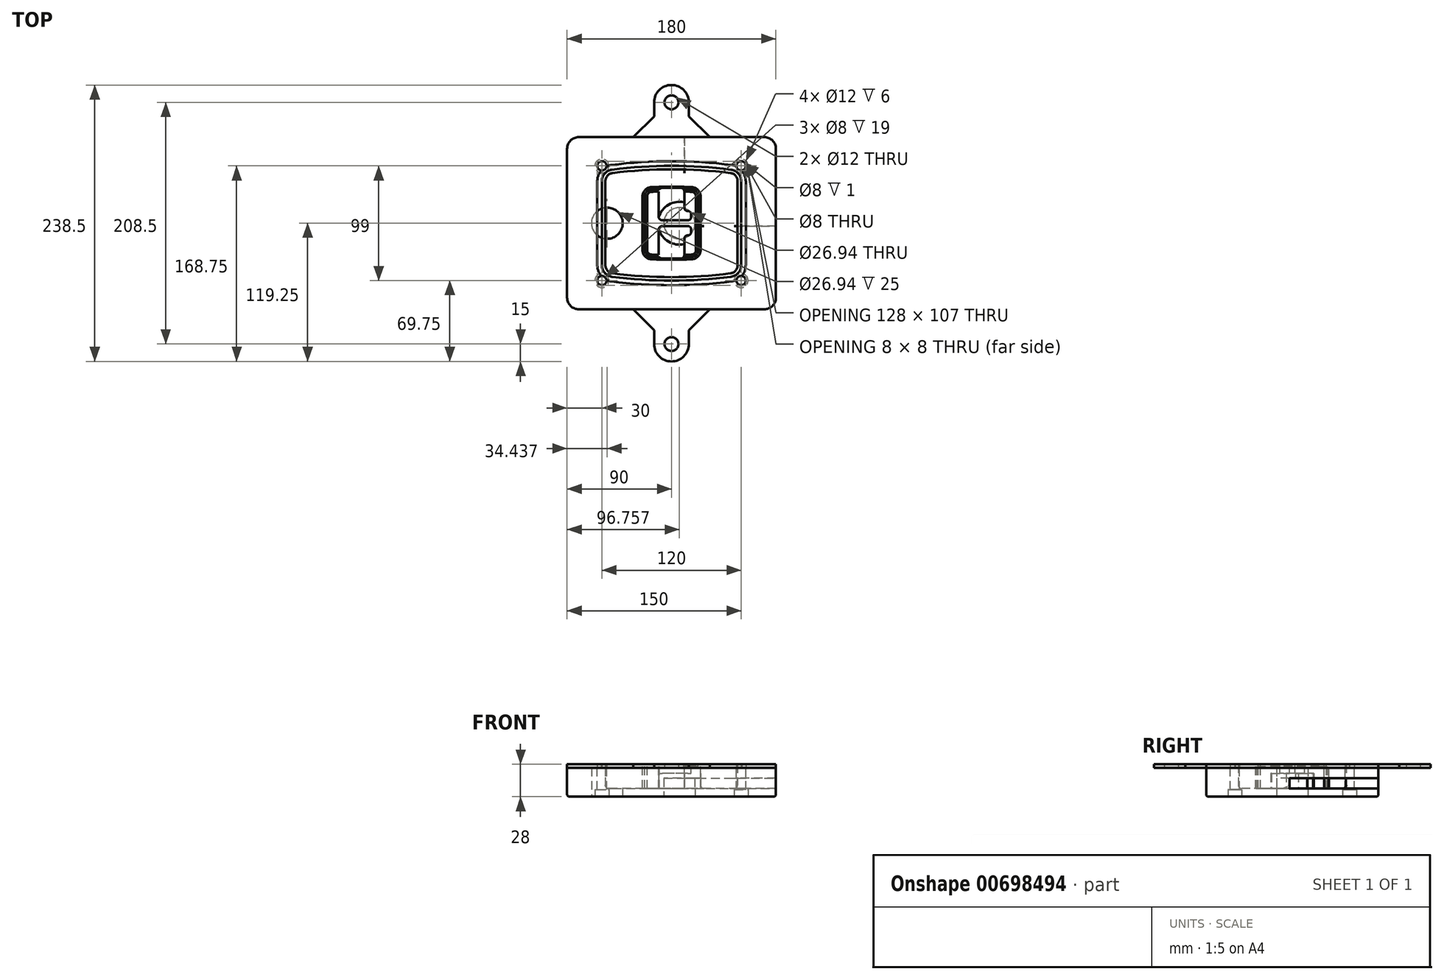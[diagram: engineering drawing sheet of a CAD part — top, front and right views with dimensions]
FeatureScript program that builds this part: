
annotation { "Feature Type Name" : "Feature", "Feature Type Description" : "" }
export const myFeature = defineFeature(function(context is Context, id is Id, definition is map)
    precondition{}
    {
        {
            var Q0;
            Q0=qCreatedBy(makeId("Top.planeOp"),FACE);
            var sketch = newSketch(context, id + "F0", { "sketchPlane" : qUnion([Q0])});
            skPoint(sketch, "E0.rect.middle", {"position": v(0, 0) * mm});
            skLineSegment(sketch, "E1.bottom", {"start": v(-80, -74.25) * mm, "end": v(80, -74.25) * mm});
            skLineSegment(sketch, "E1.top", {"start": v(-80, 74.25) * mm, "end": v(80, 74.25) * mm});
            skLineSegment(sketch, "E1.left", {"start": v(-90, -64.25) * mm, "end": v(-90, 64.25) * mm});
            skLineSegment(sketch, "E1.right", {"start": v(90, -64.25) * mm, "end": v(90, 64.25) * mm});
            skLineSegment(sketch, "E2", {"start": v(-90, 74.25) * mm, "end": v(90, -74.25) * mm, "construction": true});
            skLineSegment(sketch, "E3", {"start": v(90, 74.25) * mm, "end": v(-90, -74.25) * mm, "construction": true});
            skCircle(sketch, "E4", {"center": v(-60, 49.5) * mm, "radius": 4 * mm});
            skCircle(sketch, "E5", {"center": v(60, 49.5) * mm, "radius": 4 * mm});
            skCircle(sketch, "E6", {"center": v(60, -49.5) * mm, "radius": 4 * mm});
            skCircle(sketch, "E7", {"center": v(-60, -49.5) * mm, "radius": 4 * mm});
            skLineSegment(sketch, "E8", {"start": v(-60, 49.5) * mm, "end": v(60, 49.5) * mm, "construction": true});
            skLineSegment(sketch, "E9", {"start": v(60, 49.5) * mm, "end": v(60, -49.5) * mm, "construction": true});
            skLineSegment(sketch, "E10", {"start": v(60, -49.5) * mm, "end": v(-60, -49.5) * mm, "construction": true});
            skLineSegment(sketch, "E11", {"start": v(-60, -49.5) * mm, "end": v(-60, 49.5) * mm, "construction": true});
            skLineSegment(sketch, "E12", {"start": v(-60, 36.3) * mm, "end": v(-60, -36.3) * mm});
            skLineSegment(sketch, "E13", {"start": v(60, 36.3) * mm, "end": v(60, -36.3) * mm});
            skArc(sketch, "E14", {"start": v(51.27, 46.22) * mm, "mid": v(0, 49.5) * mm, "end": v(-51.27, 46.22) * mm});
            skArc(sketch, "E15", {"start": v(-51.27, -46.22) * mm, "mid": v(0, -49.5) * mm, "end": v(51.27, -46.22) * mm});
            skLineSegment(sketch, "E16", {"start": v(-60, 0) * mm, "end": v(60, 0) * mm, "construction": true});
            skPoint(sketch, "E17.visualSharp", {"position": v(-60, -45) * mm});
            skArc(sketch, "E17.filletArc", {"start": v(-60, -36.3) * mm, "mid": v(-57.5, -42.9) * mm, "end": v(-51.27, -46.22) * mm});
            skPoint(sketch, "E18.visualSharp", {"position": v(-60, 45) * mm});
            skArc(sketch, "E18.filletArc", {"start": v(-51.27, 46.22) * mm, "mid": v(-57.5, 42.9) * mm, "end": v(-60, 36.3) * mm});
            skPoint(sketch, "E19.visualSharp", {"position": v(60, 45) * mm});
            skArc(sketch, "E19.filletArc", {"start": v(60, 36.3) * mm, "mid": v(57.5, 42.9) * mm, "end": v(51.27, 46.22) * mm});
            skPoint(sketch, "E20.visualSharp", {"position": v(60, -45) * mm});
            skArc(sketch, "E20.filletArc", {"start": v(51.27, -46.22) * mm, "mid": v(57.5, -42.9) * mm, "end": v(60, -36.3) * mm});
            skPoint(sketch, "E21.visualSharp", {"position": v(-90, 74.25) * mm});
            skArc(sketch, "E21.filletArc", {"start": v(-80, 74.25) * mm, "mid": v(-87.07, 71.32) * mm, "end": v(-90, 64.25) * mm});
            skPoint(sketch, "E22.visualSharp", {"position": v(90, 74.25) * mm});
            skArc(sketch, "E22.filletArc", {"start": v(90, 64.25) * mm, "mid": v(87.07, 71.32) * mm, "end": v(80, 74.25) * mm});
            skPoint(sketch, "E23.visualSharp", {"position": v(90, -74.25) * mm});
            skArc(sketch, "E23.filletArc", {"start": v(80, -74.25) * mm, "mid": v(87.07, -71.32) * mm, "end": v(90, -64.25) * mm});
            skPoint(sketch, "E24.visualSharp", {"position": v(-90, -74.25) * mm});
            skArc(sketch, "E24.filletArc", {"start": v(-90, -64.25) * mm, "mid": v(-87.07, -71.32) * mm, "end": v(-80, -74.25) * mm});
            skArc(sketch, "E25.0", {"start": v(57, 36.3) * mm, "mid": v(55.26, 40.92) * mm, "end": v(50.9, 43.24) * mm});
            skLineSegment(sketch, "E25.1", {"start": v(57, 36.3) * mm, "end": v(57, -36.3) * mm});
            skArc(sketch, "E25.2", {"start": v(50.9, -43.24) * mm, "mid": v(55.26, -40.92) * mm, "end": v(57, -36.3) * mm});
            skArc(sketch, "E25.3", {"start": v(-50.9, -43.24) * mm, "mid": v(0, -46.5) * mm, "end": v(50.9, -43.24) * mm});
            skArc(sketch, "E25.4", {"start": v(-57, -36.3) * mm, "mid": v(-55.26, -40.92) * mm, "end": v(-50.9, -43.24) * mm});
            skArc(sketch, "E25.5", {"start": v(50.9, 43.24) * mm, "mid": v(0, 46.5) * mm, "end": v(-50.9, 43.24) * mm});
            skLineSegment(sketch, "E25.6", {"start": v(-57, 36.3) * mm, "end": v(-57, -36.3) * mm});
            skArc(sketch, "E25.7", {"start": v(-50.9, 43.24) * mm, "mid": v(-55.26, 40.92) * mm, "end": v(-57, 36.3) * mm});
            skArc(sketch, "E26.0", {"start": v(-51.78, 50.19) * mm, "mid": v(-60.51, 45.55) * mm, "end": v(-64, 36.3) * mm});
            skArc(sketch, "E26.1", {"start": v(51.78, 50.19) * mm, "mid": v(0, 53.5) * mm, "end": v(-51.78, 50.19) * mm});
            skArc(sketch, "E26.2", {"start": v(64, 36.3) * mm, "mid": v(60.51, 45.55) * mm, "end": v(51.78, 50.19) * mm});
            skLineSegment(sketch, "E26.3", {"start": v(64, 36.3) * mm, "end": v(64, -36.3) * mm});
            skArc(sketch, "E26.4", {"start": v(51.78, -50.19) * mm, "mid": v(60.51, -45.55) * mm, "end": v(64, -36.3) * mm});
            skLineSegment(sketch, "E26.5", {"start": v(-64, 36.3) * mm, "end": v(-64, -36.3) * mm});
            skArc(sketch, "E26.6", {"start": v(-51.78, -50.19) * mm, "mid": v(0, -53.5) * mm, "end": v(51.78, -50.19) * mm});
            skArc(sketch, "E26.7", {"start": v(-64, -36.3) * mm, "mid": v(-60.51, -45.55) * mm, "end": v(-51.78, -50.19) * mm});
            skSolve(sketch);
        }
        {
            var Q0;
            Q0=makeQuery(id+"F0.imprint","IMPRINT",FACE,{"disambiguationData":[TD([[makeQuery(id+"F0.imprint","IMPRINT",EDGE,{"derivedFrom":sQuery(id+"F0.wireOp",EDGE,"E1.bottom")}),1.0]])]});
            var Q1;
            Q1=makeQuery(id+"F0.imprint","IMPRINT",FACE,{"disambiguationData":[TD([[makeQuery(id+"F0.imprint","IMPRINT",EDGE,{"derivedFrom":sQuery(id+"F0.wireOp",EDGE,"E12")}),1.0]])]});
            var Q2;
            Q2=makeQuery(id+"F0.imprint","IMPRINT",FACE,{"disambiguationData":[TD([[makeQuery(id+"F0.imprint","IMPRINT",EDGE,{"derivedFrom":sQuery(id+"F0.wireOp",EDGE,"E25.0")}),1.0]])]});
            var Q3;
            Q3=makeQuery(id+"F0.imprint","IMPRINT",FACE,{"disambiguationData":[TD([[makeQuery(id+"F0.imprint","IMPRINT",EDGE,{"derivedFrom":sQuery(id+"F0.wireOp",EDGE,"E12")}),-1.0]])]});
            extrude(context, id + "F1", {"entities" : qUnion([Q0, Q1, Q2, Q3]), "oppositeDirection" : true, "depth" : 25 * mm});
        }
        {
            var Q0;
            Q0=makeQuery(id+"F0.imprint","IMPRINT",FACE,{"disambiguationData":[TD([[makeQuery(id+"F0.imprint","IMPRINT",EDGE,{"derivedFrom":sQuery(id+"F0.wireOp",EDGE,"E12")}),1.0]])]});
            extrude(context, id + "F2", {"entities" : qUnion([Q0]), "operationType" : NewBodyOperationType.ADD, "depth" : 3 * mm});
        }
        {
            var Q0;
            Q0=makeQuery(id+"F0.imprint","IMPRINT",FACE,{"disambiguationData":[TD([[makeQuery(id+"F0.imprint","IMPRINT",EDGE,{"derivedFrom":sQuery(id+"F0.wireOp",EDGE,"E25.0")}),1.0]])]});
            extrude(context, id + "F3", {"entities" : qUnion([Q0]), "operationType" : NewBodyOperationType.REMOVE, "oppositeDirection" : true, "depth" : 18 * mm});
        }
        {
            var Q0;
            Q0=makeQuery(id+"F2.opExtrude","CAP_FACE",FACE,{"disambiguationData":[OSD([sQuery(id+"F0.wireOp",EDGE,"E12"),sQuery(id+"F0.wireOp",EDGE,"E13"),sQuery(id+"F0.wireOp",EDGE,"E14"),sQuery(id+"F0.wireOp",EDGE,"E15"),sQuery(id+"F0.wireOp",EDGE,"E17.filletArc"),sQuery(id+"F0.wireOp",EDGE,"E18.filletArc"),sQuery(id+"F0.wireOp",EDGE,"E19.filletArc"),sQuery(id+"F0.wireOp",EDGE,"E20.filletArc"),sQuery(id+"F0.wireOp",EDGE,"E25.0"),sQuery(id+"F0.wireOp",EDGE,"E25.1"),sQuery(id+"F0.wireOp",EDGE,"E25.2"),sQuery(id+"F0.wireOp",EDGE,"E25.3"),sQuery(id+"F0.wireOp",EDGE,"E25.4"),sQuery(id+"F0.wireOp",EDGE,"E25.5"),sQuery(id+"F0.wireOp",EDGE,"E25.6"),sQuery(id+"F0.wireOp",EDGE,"E25.7")])],"isStart":false});
            var sketch = newSketch(context, id + "F4", { "sketchPlane" : qUnion([Q0])});
            skArc(sketch, "E27.0", {"start": v(-17.36, -31.1) * mm, "mid": v(0, -31.5) * mm, "end": v(17.36, -31.1) * mm});
            skArc(sketch, "E28.0", {"start": v(17.36, 31.1) * mm, "mid": v(0, 31.5) * mm, "end": v(-17.36, 31.1) * mm});
            skLineSegment(sketch, "E29", {"start": v(-25, 23.12) * mm, "end": v(-25, -23.12) * mm});
            skLineSegment(sketch, "E30", {"start": v(25, 23.12) * mm, "end": v(25, -23.12) * mm});
            skLineSegment(sketch, "E31", {"start": v(-25, 30.69) * mm, "end": v(25, 30.69) * mm, "construction": true});
            skLineSegment(sketch, "E32", {"start": v(-25, -30.69) * mm, "end": v(25, -30.69) * mm, "construction": true});
            skPoint(sketch, "E33.visualSharp", {"position": v(-25, 30.69) * mm});
            skArc(sketch, "E33.filletArc", {"start": v(-17.36, 31.1) * mm, "mid": v(-22.78, 28.64) * mm, "end": v(-25, 23.12) * mm});
            skPoint(sketch, "E34.visualSharp", {"position": v(25, 30.69) * mm});
            skArc(sketch, "E34.filletArc", {"start": v(25, 23.12) * mm, "mid": v(22.78, 28.64) * mm, "end": v(17.36, 31.1) * mm});
            skPoint(sketch, "E35.visualSharp", {"position": v(25, -30.69) * mm});
            skArc(sketch, "E35.filletArc", {"start": v(17.36, -31.1) * mm, "mid": v(22.78, -28.64) * mm, "end": v(25, -23.12) * mm});
            skPoint(sketch, "E36.visualSharp", {"position": v(-25, -30.69) * mm});
            skArc(sketch, "E36.filletArc", {"start": v(-25, -23.12) * mm, "mid": v(-22.78, -28.64) * mm, "end": v(-17.36, -31.1) * mm});
            skArc(sketch, "E37.0", {"start": v(50.9, 43.24) * mm, "mid": v(0, 46.5) * mm, "end": v(-50.9, 43.24) * mm});
            skArc(sketch, "E37.1", {"start": v(-50.9, 43.24) * mm, "mid": v(-55.26, 40.92) * mm, "end": v(-57, 36.3) * mm});
            skLineSegment(sketch, "E37.2", {"start": v(-57, 36.3) * mm, "end": v(-57, -36.3) * mm});
            skArc(sketch, "E37.3", {"start": v(-57, -36.3) * mm, "mid": v(-55.26, -40.92) * mm, "end": v(-50.9, -43.24) * mm});
            skArc(sketch, "E37.4", {"start": v(-50.9, -43.24) * mm, "mid": v(0, -46.5) * mm, "end": v(50.9, -43.24) * mm});
            skArc(sketch, "E37.5", {"start": v(50.9, -43.24) * mm, "mid": v(55.26, -40.92) * mm, "end": v(57, -36.3) * mm});
            skLineSegment(sketch, "E37.6", {"start": v(57, 36.3) * mm, "end": v(57, -36.3) * mm});
            skArc(sketch, "E37.7", {"start": v(57, 36.3) * mm, "mid": v(55.26, 40.92) * mm, "end": v(50.9, 43.24) * mm});
            skLineSegment(sketch, "E38.0", {"start": v(23, 23.12) * mm, "end": v(23, -23.12) * mm});
            skArc(sketch, "E38.1", {"start": v(17.27, -29.1) * mm, "mid": v(21.34, -27.26) * mm, "end": v(23, -23.12) * mm});
            skArc(sketch, "E38.2", {"start": v(-17.27, -29.1) * mm, "mid": v(0, -29.5) * mm, "end": v(17.27, -29.1) * mm});
            skArc(sketch, "E38.3", {"start": v(-23, -23.12) * mm, "mid": v(-21.34, -27.26) * mm, "end": v(-17.27, -29.1) * mm});
            skLineSegment(sketch, "E38.4", {"start": v(-23, 23.12) * mm, "end": v(-23, -23.12) * mm});
            skArc(sketch, "E38.5", {"start": v(23, 23.12) * mm, "mid": v(21.34, 27.26) * mm, "end": v(17.27, 29.1) * mm});
            skArc(sketch, "E38.6", {"start": v(-17.27, 29.1) * mm, "mid": v(-21.34, 27.26) * mm, "end": v(-23, 23.12) * mm});
            skArc(sketch, "E38.7", {"start": v(17.27, 29.1) * mm, "mid": v(0, 29.5) * mm, "end": v(-17.27, 29.1) * mm});
            skArc(sketch, "E39.0", {"start": v(21, 23.12) * mm, "mid": v(19.9, 25.88) * mm, "end": v(17.18, 27.11) * mm});
            skLineSegment(sketch, "E39.1", {"start": v(21, 23.12) * mm, "end": v(21, -23.12) * mm});
            skArc(sketch, "E39.2", {"start": v(17.18, -27.11) * mm, "mid": v(19.9, -25.88) * mm, "end": v(21, -23.12) * mm});
            skArc(sketch, "E39.3", {"start": v(-17.18, -27.11) * mm, "mid": v(0, -27.5) * mm, "end": v(17.18, -27.11) * mm});
            skArc(sketch, "E39.4", {"start": v(-21, -23.12) * mm, "mid": v(-19.9, -25.88) * mm, "end": v(-17.18, -27.11) * mm});
            skArc(sketch, "E39.5", {"start": v(17.18, 27.11) * mm, "mid": v(0, 27.5) * mm, "end": v(-17.18, 27.11) * mm});
            skLineSegment(sketch, "E39.6", {"start": v(-21, 23.12) * mm, "end": v(-21, -23.12) * mm});
            skArc(sketch, "E39.7", {"start": v(-17.18, 27.11) * mm, "mid": v(-19.9, 25.88) * mm, "end": v(-21, 23.12) * mm});
            skLineSegment(sketch, "E40", {"start": v(-25, 0) * mm, "end": v(25, 0) * mm, "construction": true});
            skLineSegment(sketch, "E41", {"start": v(-11, 5.5) * mm, "end": v(-11, 27.5) * mm});
            skLineSegment(sketch, "E42", {"start": v(-8, 30.5) * mm, "end": v(8, 30.5) * mm});
            skLineSegment(sketch, "E43", {"start": v(11, 27.5) * mm, "end": v(11, 13.5) * mm});
            skLineSegment(sketch, "E44", {"start": v(14, 10.5) * mm, "end": v(14, 10.5) * mm});
            skLineSegment(sketch, "E45", {"start": v(17, 7.5) * mm, "end": v(17, 5.5) * mm});
            skLineSegment(sketch, "E46", {"start": v(14, 2.5) * mm, "end": v(-8, 2.5) * mm});
            skPoint(sketch, "E47.visualSharp", {"position": v(-11, 30.5) * mm});
            skArc(sketch, "E47.filletArc", {"start": v(-8, 30.5) * mm, "mid": v(-10.12, 29.62) * mm, "end": v(-11, 27.5) * mm});
            skPoint(sketch, "E48.visualSharp", {"position": v(11, 30.5) * mm});
            skArc(sketch, "E48.filletArc", {"start": v(11, 27.5) * mm, "mid": v(10.12, 29.62) * mm, "end": v(8, 30.5) * mm});
            skPoint(sketch, "E49.visualSharp", {"position": v(11, 10.5) * mm});
            skArc(sketch, "E49.filletArc", {"start": v(11, 13.5) * mm, "mid": v(11.88, 11.38) * mm, "end": v(14, 10.5) * mm});
            skPoint(sketch, "E50.visualSharp", {"position": v(17, 10.5) * mm});
            skArc(sketch, "E50.filletArc", {"start": v(17, 7.5) * mm, "mid": v(16.12, 9.62) * mm, "end": v(14, 10.5) * mm});
            skPoint(sketch, "E51.visualSharp", {"position": v(17, 2.5) * mm});
            skArc(sketch, "E51.filletArc", {"start": v(14, 2.5) * mm, "mid": v(16.12, 3.38) * mm, "end": v(17, 5.5) * mm});
            skPoint(sketch, "E52.visualSharp", {"position": v(-11, 2.5) * mm});
            skArc(sketch, "E52.filletArc", {"start": v(-11, 5.5) * mm, "mid": v(-10.12, 3.38) * mm, "end": v(-8, 2.5) * mm});
            skLineSegment(sketch, "E53.0.MirrorCS", {"start": v(14, -2.5) * mm, "end": v(-8, -2.5) * mm});
            skArc(sketch, "E54.0.MirrorCS", {"start": v(-11, -5.5) * mm, "mid": v(-10.12, -3.38) * mm, "end": v(-8, -2.5) * mm});
            skLineSegment(sketch, "E55.0.MirrorCS", {"start": v(-11, -5.5) * mm, "end": v(-11, -27.5) * mm});
            skArc(sketch, "E56.0.MirrorCS", {"start": v(-8, -30.5) * mm, "mid": v(-10.12, -29.62) * mm, "end": v(-11, -27.5) * mm});
            skLineSegment(sketch, "E57.0.MirrorCS", {"start": v(-8, -30.5) * mm, "end": v(8, -30.5) * mm});
            skArc(sketch, "E58.0.MirrorCS", {"start": v(11, -27.5) * mm, "mid": v(10.12, -29.62) * mm, "end": v(8, -30.5) * mm});
            skLineSegment(sketch, "E59.0.MirrorCS", {"start": v(11, -27.5) * mm, "end": v(11, -13.5) * mm});
            skArc(sketch, "E60.0.MirrorCS", {"start": v(11, -13.5) * mm, "mid": v(11.88, -11.38) * mm, "end": v(14, -10.5) * mm});
            skArc(sketch, "E61.0.MirrorCS", {"start": v(17, -7.5) * mm, "mid": v(16.12, -9.62) * mm, "end": v(14, -10.5) * mm});
            skLineSegment(sketch, "E62.0.MirrorCS", {"start": v(17, -7.5) * mm, "end": v(17, -5.5) * mm});
            skArc(sketch, "E63.0.MirrorCS", {"start": v(14, -2.5) * mm, "mid": v(16.12, -3.38) * mm, "end": v(17, -5.5) * mm});
            skSolve(sketch);
        }
        {
            var Q0;
            Q0=makeQuery(id+"F4.imprint","IMPRINT",FACE,{"disambiguationData":[TD([[makeQuery(id+"F4.imprint","IMPRINT",EDGE,{"derivedFrom":sQuery(id+"F4.wireOp",EDGE,"E27.0")}),1.0]])]});
            var Q1;
            Q1=makeQuery(id+"F4.imprint","IMPRINT",FACE,{"disambiguationData":[TD([[makeQuery(id+"F4.imprint","IMPRINT",EDGE,{"derivedFrom":sQuery(id+"F4.wireOp",EDGE,"E38.0")}),-1.0]])]});
            var Q2;
            Q2=makeQuery(id+"F4.imprint","IMPRINT",FACE,{"disambiguationData":[TD([[makeQuery(id+"F4.imprint","IMPRINT",EDGE,{"derivedFrom":sQuery(id+"F4.wireOp",EDGE,"E39.0")}),1.0]])]});
            extrude(context, id + "F5", {"entities" : qUnion([Q0, Q1, Q2]), "operationType" : NewBodyOperationType.ADD, "endBound" : BoundingType.UP_TO_NEXT, "oppositeDirection" : true, "depth" : 25 * mm});
        }
        {
            var Q0;
            Q0=makeQuery(id+"F4.imprint","IMPRINT",FACE,{"disambiguationData":[TD([[makeQuery(id+"F4.imprint","IMPRINT",EDGE,{"derivedFrom":sQuery(id+"F4.wireOp",EDGE,"E38.0")}),-1.0]])]});
            extrude(context, id + "F6", {"entities" : qUnion([Q0]), "operationType" : NewBodyOperationType.REMOVE, "oppositeDirection" : true, "depth" : 2 * mm});
        }
        {
            var Q0;
            Q0=makeQuery(id+"F1.opExtrude","CAP_FACE",FACE,{"disambiguationData":[OSD([sQuery(id+"F0.wireOp",EDGE,"E1.bottom"),sQuery(id+"F0.wireOp",EDGE,"E1.top"),sQuery(id+"F0.wireOp",EDGE,"E1.left"),sQuery(id+"F0.wireOp",EDGE,"E1.right"),sQuery(id+"F0.wireOp",EDGE,"E4"),sQuery(id+"F0.wireOp",EDGE,"E5"),sQuery(id+"F0.wireOp",EDGE,"E6"),sQuery(id+"F0.wireOp",EDGE,"E7"),sQuery(id+"F0.wireOp",EDGE,"E21.filletArc"),sQuery(id+"F0.wireOp",EDGE,"E22.filletArc"),sQuery(id+"F0.wireOp",EDGE,"E23.filletArc"),sQuery(id+"F0.wireOp",EDGE,"E24.filletArc")])],"isStart":false});
            var sketch = newSketch(context, id + "F7", { "sketchPlane" : qUnion([Q0])});
            skCircle(sketch, "E64", {"center": v(6.76, 0) * mm, "radius": 13.47 * mm});
            skCircle(sketch, "E65", {"center": v(-55.56, 0) * mm, "radius": 13.47 * mm});
            skLineSegment(sketch, "E66", {"start": v(90, 0) * mm, "end": v(-90, 0) * mm});
            skCircle(sketch, "E67", {"center": v(6.76, 0) * mm, "radius": 18.47 * mm});
            skCircle(sketch, "E68", {"center": v(60, -49.5) * mm, "radius": 6 * mm});
            skCircle(sketch, "E69", {"center": v(-60, -49.5) * mm, "radius": 6 * mm});
            skCircle(sketch, "E70", {"center": v(-60, 49.5) * mm, "radius": 6 * mm});
            skCircle(sketch, "E71", {"center": v(60, 49.5) * mm, "radius": 6 * mm});
            skSolve(sketch);
        }
        {
            var Q0;
            {var subQ1=sQuery(id+"F7.wireOp",EDGE,"E66");var subQ4=sQuery(id+"F7.wireOp",EDGE,"E64");var subQ6=makeQuery(id+"F7.imprint","INTERSECT",VERTEX,{"disambiguationData":[OD(0.0)],"derivedFrom":[subQ4,subQ1]});Q0=makeQuery(id+"F7.imprint","IMPRINT",FACE,{"disambiguationData":[TD([[makeQuery(id+"F7.imprint","IMPRINT",EDGE,{"disambiguationData":[TD([[subQ6,-1.0]])],"derivedFrom":subQ4}),-1.0]])]});}
            var Q1;
            {var subQ0=sQuery(id+"F7.wireOp",EDGE,"E66");var subQ1=sQuery(id+"F7.wireOp",EDGE,"E64");var subQ3=makeQuery(id+"F7.imprint","INTERSECT",VERTEX,{"disambiguationData":[OD(0.0)],"derivedFrom":[subQ1,subQ0]});Q1=makeQuery(id+"F7.imprint","IMPRINT",FACE,{"disambiguationData":[TD([[makeQuery(id+"F7.imprint","IMPRINT",EDGE,{"disambiguationData":[TD([[subQ3,-1.0]])],"derivedFrom":subQ1}),1.0]])]});}
            var Q2;
            {var subQ0=sQuery(id+"F7.wireOp",EDGE,"E66");var subQ1=sQuery(id+"F7.wireOp",EDGE,"E64");var subQ3=makeQuery(id+"F7.imprint","INTERSECT",VERTEX,{"disambiguationData":[OD(0.0)],"derivedFrom":[subQ1,subQ0]});Q2=makeQuery(id+"F7.imprint","IMPRINT",FACE,{"disambiguationData":[TD([[makeQuery(id+"F7.imprint","IMPRINT",EDGE,{"disambiguationData":[TD([[subQ3,1.0]])],"derivedFrom":subQ1}),1.0]])]});}
            var Q3;
            {var subQ1=sQuery(id+"F7.wireOp",EDGE,"E66");var subQ4=sQuery(id+"F7.wireOp",EDGE,"E64");var subQ6=makeQuery(id+"F7.imprint","INTERSECT",VERTEX,{"disambiguationData":[OD(0.0)],"derivedFrom":[subQ4,subQ1]});Q3=makeQuery(id+"F7.imprint","IMPRINT",FACE,{"disambiguationData":[TD([[makeQuery(id+"F7.imprint","IMPRINT",EDGE,{"disambiguationData":[TD([[subQ6,1.0]])],"derivedFrom":subQ4}),-1.0]])]});}
            extrude(context, id + "F8", {"entities" : qUnion([Q0, Q1, Q2, Q3]), "operationType" : NewBodyOperationType.ADD, "oppositeDirection" : true, "depth" : 20 * mm});
        }
        {
            var Q0;
            {var subQ0=sQuery(id+"F7.wireOp",EDGE,"E66");var subQ1=sQuery(id+"F7.wireOp",EDGE,"E64");var subQ3=makeQuery(id+"F7.imprint","INTERSECT",VERTEX,{"disambiguationData":[OD(0.0)],"derivedFrom":[subQ1,subQ0]});Q0=makeQuery(id+"F7.imprint","IMPRINT",FACE,{"disambiguationData":[TD([[makeQuery(id+"F7.imprint","IMPRINT",EDGE,{"disambiguationData":[TD([[subQ3,-1.0]])],"derivedFrom":subQ1}),1.0]])]});}
            var Q1;
            {var subQ0=sQuery(id+"F7.wireOp",EDGE,"E66");var subQ1=sQuery(id+"F7.wireOp",EDGE,"E64");var subQ3=makeQuery(id+"F7.imprint","INTERSECT",VERTEX,{"disambiguationData":[OD(0.0)],"derivedFrom":[subQ1,subQ0]});Q1=makeQuery(id+"F7.imprint","IMPRINT",FACE,{"disambiguationData":[TD([[makeQuery(id+"F7.imprint","IMPRINT",EDGE,{"disambiguationData":[TD([[subQ3,1.0]])],"derivedFrom":subQ1}),1.0]])]});}
            extrude(context, id + "F9", {"entities" : qUnion([Q0, Q1]), "operationType" : NewBodyOperationType.REMOVE, "oppositeDirection" : true, "depth" : 16 * mm});
        }
        {
            var Q0;
            {var subQ0=sQuery(id+"F7.wireOp",EDGE,"E66");var subQ1=sQuery(id+"F7.wireOp",EDGE,"E65");var subQ3=makeQuery(id+"F7.imprint","INTERSECT",VERTEX,{"disambiguationData":[OD(0.0)],"derivedFrom":[subQ1,subQ0]});Q0=makeQuery(id+"F7.imprint","IMPRINT",FACE,{"disambiguationData":[TD([[makeQuery(id+"F7.imprint","IMPRINT",EDGE,{"disambiguationData":[TD([[subQ3,-1.0]])],"derivedFrom":subQ1}),1.0]])]});}
            var Q1;
            {var subQ0=sQuery(id+"F7.wireOp",EDGE,"E66");var subQ1=sQuery(id+"F7.wireOp",EDGE,"E65");var subQ3=makeQuery(id+"F7.imprint","INTERSECT",VERTEX,{"disambiguationData":[OD(0.0)],"derivedFrom":[subQ1,subQ0]});Q1=makeQuery(id+"F7.imprint","IMPRINT",FACE,{"disambiguationData":[TD([[makeQuery(id+"F7.imprint","IMPRINT",EDGE,{"disambiguationData":[TD([[subQ3,1.0]])],"derivedFrom":subQ1}),1.0]])]});}
            extrude(context, id + "F10", {"entities" : qUnion([Q0, Q1]), "operationType" : NewBodyOperationType.REMOVE, "oppositeDirection" : true, "depth" : 25 * mm});
        }
        {
            var Q0;
            Q0=makeQuery(id+"F7.imprint","IMPRINT",FACE,{"disambiguationData":[TD([[makeQuery(id+"F7.imprint","IMPRINT",EDGE,{"derivedFrom":sQuery(id+"F7.wireOp",EDGE,"E68")}),1.0]])]});
            var Q1;
            Q1=makeQuery(id+"F7.imprint","IMPRINT",FACE,{"disambiguationData":[TD([[makeQuery(id+"F7.imprint","IMPRINT",EDGE,{"derivedFrom":makeQuery(id+"F1.opExtrude","CAP_EDGE",EDGE,{"disambiguationData":[OSD([sQuery(id+"F0.wireOp",EDGE,"E5")])],"isStart":false})}),-1.0]])]});
            var Q2;
            Q2=makeQuery(id+"F7.imprint","IMPRINT",FACE,{"disambiguationData":[TD([[makeQuery(id+"F7.imprint","IMPRINT",EDGE,{"derivedFrom":sQuery(id+"F7.wireOp",EDGE,"E69")}),1.0]])]});
            var Q3;
            Q3=makeQuery(id+"F7.imprint","IMPRINT",FACE,{"disambiguationData":[TD([[makeQuery(id+"F7.imprint","IMPRINT",EDGE,{"derivedFrom":makeQuery(id+"F1.opExtrude","CAP_EDGE",EDGE,{"disambiguationData":[OSD([sQuery(id+"F0.wireOp",EDGE,"E4")])],"isStart":false})}),-1.0]])]});
            var Q4;
            Q4=makeQuery(id+"F7.imprint","IMPRINT",FACE,{"disambiguationData":[TD([[makeQuery(id+"F7.imprint","IMPRINT",EDGE,{"derivedFrom":sQuery(id+"F7.wireOp",EDGE,"E70")}),1.0]])]});
            var Q5;
            Q5=makeQuery(id+"F7.imprint","IMPRINT",FACE,{"disambiguationData":[TD([[makeQuery(id+"F7.imprint","IMPRINT",EDGE,{"derivedFrom":makeQuery(id+"F1.opExtrude","CAP_EDGE",EDGE,{"disambiguationData":[OSD([sQuery(id+"F0.wireOp",EDGE,"E7")])],"isStart":false})}),-1.0]])]});
            var Q6;
            Q6=makeQuery(id+"F7.imprint","IMPRINT",FACE,{"disambiguationData":[TD([[makeQuery(id+"F7.imprint","IMPRINT",EDGE,{"derivedFrom":sQuery(id+"F7.wireOp",EDGE,"E71")}),1.0]])]});
            var Q7;
            Q7=makeQuery(id+"F7.imprint","IMPRINT",FACE,{"disambiguationData":[TD([[makeQuery(id+"F7.imprint","IMPRINT",EDGE,{"derivedFrom":makeQuery(id+"F1.opExtrude","CAP_EDGE",EDGE,{"disambiguationData":[OSD([sQuery(id+"F0.wireOp",EDGE,"E6")])],"isStart":false})}),-1.0]])]});
            extrude(context, id + "F11", {"entities" : qUnion([Q0, Q1, Q2, Q3, Q4, Q5, Q6, Q7]), "operationType" : NewBodyOperationType.REMOVE, "oppositeDirection" : true, "depth" : 6 * mm});
        }
        {
            var Q0;
            Q0=makeQuery(id+"F9.boolean.opBoolean","COPY",FACE,{"derivedFrom":makeQuery(id+"F9.opExtrude","CAP_FACE",FACE,{"disambiguationData":[OSD([sQuery(id+"F7.wireOp",EDGE,"E64")])],"isStart":false})});
            var sketch = newSketch(context, id + "F12", { "sketchPlane" : qUnion([Q0])});
            skArc(sketch, "E72.0", {"start": v(11, -88.19) * mm, "mid": v(97.1, -83.6) * mm, "end": v(92.5, 2.5) * mm});
            skLineSegment(sketch, "E72.1", {"start": v(11, -17.97) * mm, "end": v(11, -17.97) * mm});
            skLineSegment(sketch, "E73", {"start": v(92.5, -105.13) * mm, "end": v(102.3, -105.13) * mm});
            skLineSegment(sketch, "E74.0", {"start": v(92.5, 2.5) * mm, "end": v(14, 2.5) * mm});
            skArc(sketch, "E74.1", {"start": v(14, 2.5) * mm, "mid": v(16.12, 3.38) * mm, "end": v(17, 5.5) * mm});
            skLineSegment(sketch, "E74.2", {"start": v(17, 7.5) * mm, "end": v(17, 5.5) * mm});
            skArc(sketch, "E74.3", {"start": v(17, 7.5) * mm, "mid": v(16.12, 9.62) * mm, "end": v(14, 10.5) * mm});
            skArc(sketch, "E74.4", {"start": v(11, 13.5) * mm, "mid": v(11.88, 11.38) * mm, "end": v(14, 10.5) * mm});
            skLineSegment(sketch, "E74.5", {"start": v(11, 13.5) * mm, "end": v(11, -88.19) * mm});
            skLineSegment(sketch, "E74.7", {"start": v(92.5, -2.5) * mm, "end": v(14, -2.5) * mm});
            skArc(sketch, "E74.8", {"start": v(14, -2.5) * mm, "mid": v(16.12, -3.38) * mm, "end": v(17, -5.5) * mm});
            skLineSegment(sketch, "E74.9", {"start": v(17, -7.5) * mm, "end": v(17, -5.5) * mm});
            skArc(sketch, "E74.10", {"start": v(17, -7.5) * mm, "mid": v(16.12, -9.62) * mm, "end": v(14, -10.5) * mm});
            skArc(sketch, "E74.11", {"start": v(11, -13.5) * mm, "mid": v(11.88, -11.38) * mm, "end": v(14, -10.5) * mm});
            skLineSegment(sketch, "E74.12", {"start": v(11, -17.97) * mm, "end": v(11, -13.5) * mm});
            skPoint(sketch, "E75.orphan", {"position": v(11, -130.13) * mm});
            skPoint(sketch, "E76.orphan", {"position": v(-8, -2.5) * mm});
            skPoint(sketch, "E77.orphan", {"position": v(-8, 2.5) * mm});
            skPoint(sketch, "E78.orphan", {"position": v(11, -75.13) * mm});
            skSolve(sketch);
        }
        {
            var Q0;
            {var subQ7=sQuery(id+"F12.wireOp",EDGE,"E72.0");var subQ14=sQuery(id+"F12.wireOp",EDGE,"E72.1");var subQ16=sQuery(id+"F12.wireOp",EDGE,"E74.1");var subQ18=sQuery(id+"F12.wireOp",EDGE,"E74.8");Q0=qUnion([makeQuery(id+"F12.imprint","IMPRINT",FACE,{"disambiguationData":[TD([[makeQuery(id+"F12.imprint","IMPRINT",EDGE,{"derivedFrom":subQ7}),1.0]])]}),makeQuery(id+"F12.imprint","IMPRINT",FACE,{"disambiguationData":[TD([[makeQuery(id+"F12.imprint","IMPRINT",EDGE,{"derivedFrom":subQ14}),1.0]])]}),makeQuery(id+"F12.imprint","IMPRINT",FACE,{"disambiguationData":[TD([[makeQuery(id+"F12.imprint","IMPRINT",EDGE,{"derivedFrom":subQ16}),1.0]])]}),makeQuery(id+"F12.imprint","IMPRINT",FACE,{"disambiguationData":[TD([[makeQuery(id+"F12.imprint","IMPRINT",EDGE,{"derivedFrom":subQ18}),-1.0]])]})]);}
            var Q1;
            Q1=makeQuery(id+"F5.boolean.opBoolean","SPLIT",FACE,{"disambiguationData":[TD([makeQuery(id+"F5.opExtrude","SWEPT_FACE",FACE,{"disambiguationData":[OSD([sQuery(id+"F4.wireOp",EDGE,"E38.2")])]})])],"derivedFrom":makeQuery(id+"F3.boolean.opBoolean","COPY",FACE,{"derivedFrom":makeQuery(id+"F3.opExtrude","CAP_FACE",FACE,{"disambiguationData":[OSD([sQuery(id+"F0.wireOp",EDGE,"E25.0"),sQuery(id+"F0.wireOp",EDGE,"E25.1"),sQuery(id+"F0.wireOp",EDGE,"E25.2"),sQuery(id+"F0.wireOp",EDGE,"E25.3"),sQuery(id+"F0.wireOp",EDGE,"E25.4"),sQuery(id+"F0.wireOp",EDGE,"E25.5"),sQuery(id+"F0.wireOp",EDGE,"E25.6"),sQuery(id+"F0.wireOp",EDGE,"E25.7")])],"isStart":false})})});
            extrude(context, id + "F13", {"entities" : qUnion([Q0]), "operationType" : NewBodyOperationType.REMOVE, "endBound" : BoundingType.UP_TO_SURFACE, "endBoundEntityFace" : qUnion([Q1]), "depth" : 25 * mm});
        }
        {
            var Q0;
            Q0=makeQuery(id+"F3.boolean.opBoolean","COPY",EDGE,{"derivedFrom":makeQuery(id+"F3.opExtrude","CAP_EDGE",EDGE,{"disambiguationData":[OSD([sQuery(id+"F0.wireOp",EDGE,"E25.6")])],"isStart":false})});
            var Q1;
            Q1=makeQuery(id+"F8.boolean.opBoolean","INTERSECT",EDGE,{"derivedFrom":[makeQuery(id+"F5.opExtrude","SWEPT_FACE",FACE,{"disambiguationData":[OSD([sQuery(id+"F4.wireOp",EDGE,"E30")])]}),makeQuery(id+"F8.opExtrude","CAP_FACE",FACE,{"disambiguationData":[OSD([sQuery(id+"F7.wireOp",EDGE,"E67")])],"isStart":false})]});
            var Q2;
            Q2=makeQuery(id+"F8.boolean.opBoolean","INTERSECT",EDGE,{"disambiguationData":[OD(1.0)],"derivedFrom":[makeQuery(id+"F5.opExtrude","SWEPT_FACE",FACE,{"disambiguationData":[OSD([sQuery(id+"F4.wireOp",EDGE,"E30")])]}),makeQuery(id+"F8.opExtrude","SWEPT_FACE",FACE,{"disambiguationData":[OSD([sQuery(id+"F7.wireOp",EDGE,"E67")])]})]});
            var Q3;
            {var subQ0=sQuery(id+"F4.wireOp",EDGE,"E30");Q3=makeQuery(id+"F8.boolean.opBoolean","SPLIT",EDGE,{"disambiguationData":[TD([makeQuery(id+"F5.opExtrude","SWEPT_FACE",FACE,{"disambiguationData":[OSD([sQuery(id+"F4.wireOp",EDGE,"E35.filletArc")])]})])],"derivedFrom":makeQuery(id+"F5.opExtrude","CAP_EDGE",EDGE,{"disambiguationData":[OSD([subQ0])],"isStart":false})});}
            var Q4;
            {var subQ0=sQuery(id+"F0.wireOp",EDGE,"E25.7");var subQ1=sQuery(id+"F0.wireOp",EDGE,"E25.1");var subQ2=sQuery(id+"F0.wireOp",EDGE,"E25.6");var subQ3=sQuery(id+"F0.wireOp",EDGE,"E25.5");var subQ4=sQuery(id+"F0.wireOp",EDGE,"E25.4");var subQ5=sQuery(id+"F0.wireOp",EDGE,"E25.0");var subQ6=sQuery(id+"F0.wireOp",EDGE,"E25.2");var subQ7=sQuery(id+"F0.wireOp",EDGE,"E25.3");Q4=makeQuery(id+"F8.boolean.opBoolean","INTERSECT",EDGE,{"derivedFrom":[makeQuery(id+"F5.boolean.opBoolean","SPLIT",FACE,{"disambiguationData":[TD([makeQuery(id+"F2.opExtrude","SWEPT_FACE",FACE,{"disambiguationData":[OSD([subQ5])]})])],"derivedFrom":makeQuery(id+"F3.boolean.opBoolean","COPY",FACE,{"derivedFrom":makeQuery(id+"F3.opExtrude","CAP_FACE",FACE,{"disambiguationData":[OSD([subQ5,subQ1,subQ6,subQ7,subQ4,subQ3,subQ2,subQ0])],"isStart":false})})}),makeQuery(id+"F8.opExtrude","SWEPT_FACE",FACE,{"disambiguationData":[OSD([sQuery(id+"F7.wireOp",EDGE,"E67")])]})]});}
            var Q5;
            Q5=makeQuery(id+"F8.boolean.opBoolean","INTERSECT",EDGE,{"disambiguationData":[OD(0.0)],"derivedFrom":[makeQuery(id+"F5.opExtrude","SWEPT_FACE",FACE,{"disambiguationData":[OSD([sQuery(id+"F4.wireOp",EDGE,"E30")])]}),makeQuery(id+"F8.opExtrude","SWEPT_FACE",FACE,{"disambiguationData":[OSD([sQuery(id+"F7.wireOp",EDGE,"E67")])]})]});
            fillet(context, id + "F14", {"entities" : qUnion([Q0, Q1, Q2, Q3, Q4, Q5]), "radius" : 3 * mm, "tangentPropagation" : true, "allowEdgeOverflow" : false});
        }
        {
            var Q0;
            Q0=makeQuery(id+"F1.opExtrude","CAP_EDGE",EDGE,{"disambiguationData":[OSD([sQuery(id+"F0.wireOp",EDGE,"E1.bottom")])],"isStart":false});
            fillet(context, id + "F15", {"entities" : qUnion([Q0]), "radius" : 2 * mm, "tangentPropagation" : true, "allowEdgeOverflow" : false});
        }
        {
            var Q0;
            {var subQ0=sQuery(id+"F0.wireOp",EDGE,"E21.filletArc");var subQ1=sQuery(id+"F0.wireOp",EDGE,"E7");var subQ2=sQuery(id+"F0.wireOp",EDGE,"E6");var subQ3=sQuery(id+"F0.wireOp",EDGE,"E5");var subQ4=sQuery(id+"F0.wireOp",EDGE,"E4");var subQ5=sQuery(id+"F0.wireOp",EDGE,"E22.filletArc");var subQ6=sQuery(id+"F0.wireOp",EDGE,"E1.bottom");var subQ7=sQuery(id+"F0.wireOp",EDGE,"E1.right");var subQ8=sQuery(id+"F0.wireOp",EDGE,"E1.top");var subQ9=sQuery(id+"F0.wireOp",EDGE,"E1.left");var subQ10=sQuery(id+"F0.wireOp",EDGE,"E23.filletArc");var subQ11=sQuery(id+"F0.wireOp",EDGE,"E24.filletArc");Q0=makeQuery(id+"F2.boolean.opBoolean","SPLIT",FACE,{"disambiguationData":[TD([makeQuery(id+"F1.opExtrude","SWEPT_FACE",FACE,{"disambiguationData":[OSD([subQ6])]})])],"derivedFrom":makeQuery(id+"F1.opExtrude","CAP_FACE",FACE,{"disambiguationData":[OSD([subQ6,subQ8,subQ9,subQ7,subQ4,subQ3,subQ2,subQ1,subQ0,subQ5,subQ10,subQ11])],"isStart":true})});}
            var sketch = newSketch(context, id + "F16", { "sketchPlane" : qUnion([Q0])});
            skLineSegment(sketch, "E79", {"start": v(0, 74.25) * mm, "end": v(0, 104.25) * mm, "construction": true});
            skCircle(sketch, "E80", {"center": v(0, 104.25) * mm, "radius": 6 * mm});
            skArc(sketch, "E81", {"start": v(-15, 104.25) * mm, "mid": v(0, 119.25) * mm, "end": v(15, 104.25) * mm});
            skLineSegment(sketch, "E82", {"start": v(-15, 104.25) * mm, "end": v(-15, 92.25) * mm});
            skLineSegment(sketch, "E83", {"start": v(15, 104.25) * mm, "end": v(15, 92.25) * mm});
            skLineSegment(sketch, "E84", {"start": v(15, 92.25) * mm, "end": v(33, 74.25) * mm});
            skLineSegment(sketch, "E85", {"start": v(-15, 92.25) * mm, "end": v(-33, 74.25) * mm});
            skLineSegment(sketch, "E86", {"start": v(-90, 0) * mm, "end": v(90, 0) * mm, "construction": true});
            skArc(sketch, "E87.MirrorCS", {"start": v(-15, -104.25) * mm, "mid": v(0, -119.25) * mm, "end": v(15, -104.25) * mm});
            skLineSegment(sketch, "E88.MirrorCS", {"start": v(15, -104.25) * mm, "end": v(15, -92.25) * mm});
            skLineSegment(sketch, "E89.MirrorCS", {"start": v(-15, -104.25) * mm, "end": v(-15, -92.25) * mm});
            skLineSegment(sketch, "E90.MirrorCS", {"start": v(-15, -92.25) * mm, "end": v(-33, -74.25) * mm});
            skLineSegment(sketch, "E91.MirrorCS", {"start": v(15, -92.25) * mm, "end": v(33, -74.25) * mm});
            skLineSegment(sketch, "E92.MirrorCS", {"start": v(0, -74.25) * mm, "end": v(0, -104.25) * mm, "construction": true});
            skCircle(sketch, "E93.MirrorC", {"center": v(0, -104.25) * mm, "radius": 6 * mm});
            skSolve(sketch);
        }
        {
            var Q0;
            Q0=makeQuery(id+"F0.imprint","IMPRINT",FACE,{"disambiguationData":[TD([[makeQuery(id+"F0.imprint","IMPRINT",EDGE,{"derivedFrom":sQuery(id+"F0.wireOp",EDGE,"E1.bottom")}),1.0]])]});
            var Q1;
            Q1=makeQuery(id+"F16.imprint","IMPRINT",FACE,{"disambiguationData":[TD([[makeQuery(id+"F16.imprint","IMPRINT",EDGE,{"derivedFrom":sQuery(id+"F16.wireOp",EDGE,"E80")}),-1.0]])]});
            var Q2;
            Q2=makeQuery(id+"F16.imprint","IMPRINT",FACE,{"disambiguationData":[TD([[makeQuery(id+"F16.imprint","IMPRINT",EDGE,{"derivedFrom":sQuery(id+"F16.wireOp",EDGE,"E87.MirrorCS")}),1.0]])]});
            var Q3;
            Q3=makeQuery(id+"F2.opExtrude","CAP_FACE",FACE,{"disambiguationData":[OSD([sQuery(id+"F0.wireOp",EDGE,"E12"),sQuery(id+"F0.wireOp",EDGE,"E13"),sQuery(id+"F0.wireOp",EDGE,"E14"),sQuery(id+"F0.wireOp",EDGE,"E15"),sQuery(id+"F0.wireOp",EDGE,"E17.filletArc"),sQuery(id+"F0.wireOp",EDGE,"E18.filletArc"),sQuery(id+"F0.wireOp",EDGE,"E19.filletArc"),sQuery(id+"F0.wireOp",EDGE,"E20.filletArc"),sQuery(id+"F0.wireOp",EDGE,"E25.0"),sQuery(id+"F0.wireOp",EDGE,"E25.1"),sQuery(id+"F0.wireOp",EDGE,"E25.2"),sQuery(id+"F0.wireOp",EDGE,"E25.3"),sQuery(id+"F0.wireOp",EDGE,"E25.4"),sQuery(id+"F0.wireOp",EDGE,"E25.5"),sQuery(id+"F0.wireOp",EDGE,"E25.6"),sQuery(id+"F0.wireOp",EDGE,"E25.7")])],"isStart":false});
            extrude(context, id + "F17", {"entities" : qUnion([Q0, Q1, Q2]), "endBound" : BoundingType.UP_TO_SURFACE, "depth" : 25.4 * mm, "endBoundEntityFace" : qUnion([Q3]), "offsetDistance" : 25.4 * mm});
        }
    });
